# Revit family: Table-Teknion-Zones_ZNTWE-R2015
name_source: partatom
category: Furniture
revit_build: Autodesk Revit 2015 (Build: 20140223_1515(x64)
units: mm (PartAtom-declared; Revit-internal decimal feet)

## types (4) — shared parameters
Apparent Load = 0 VA
Assembly Code = E2020200
Height = 19"
Leg Depth = 37 3/32"
Leg Width = 37 3/32"
Manufacturer = Teknion
Manufacturer Fax = 416.661.4586
Number of Poles = 1
Part Number = ZNTWE
Product Documentation Link = http://www.teknion.com
Product Line = Zones
Product Page URL = http://www.teknion.com
Series = Zones
Sustainability Data = http://www.teknion.com
Table Diameter = 54"
URL = http://www.teknion.com
Warranty = http://www.teknion.com

## per-type parameters (varying)
| type | Connector Description | Depth | Description | Model | Voltage | Width | With Power Pill 2 Modules | With Power Pill 4 Modules |
| Table 42" | Without Power Connector | 42" | Square Lounge Workshop Table, 42"d, without Cut-Out | ZNTWE42N | 0 V | 42" | No | No |
| Table 42", with Power Pill | With Power Connector | 42" | Square Lounge Workshop Table, 42"d, with Center Pill Cut-Out | ZNTWE42P | 120 V | 42" | Yes | No |
| Table 48" | Without Power Connector | 48" | Square Lounge Workshop Table, 48"d, without Cut-Out | ZNTWE48N | 0 V | 48" | No | No |
| Table 48", with Power Pill | With Power Connector | 48" | Square Lounge Workshop Table, 48"d, with Center Pill Cut-Out | ZNTWE48P | 120 V | 48" | No | Yes |

## geometry (parser evidence)
native form markers: Blend x158, Sweep x9
no freeform markers — native parametric forms only
